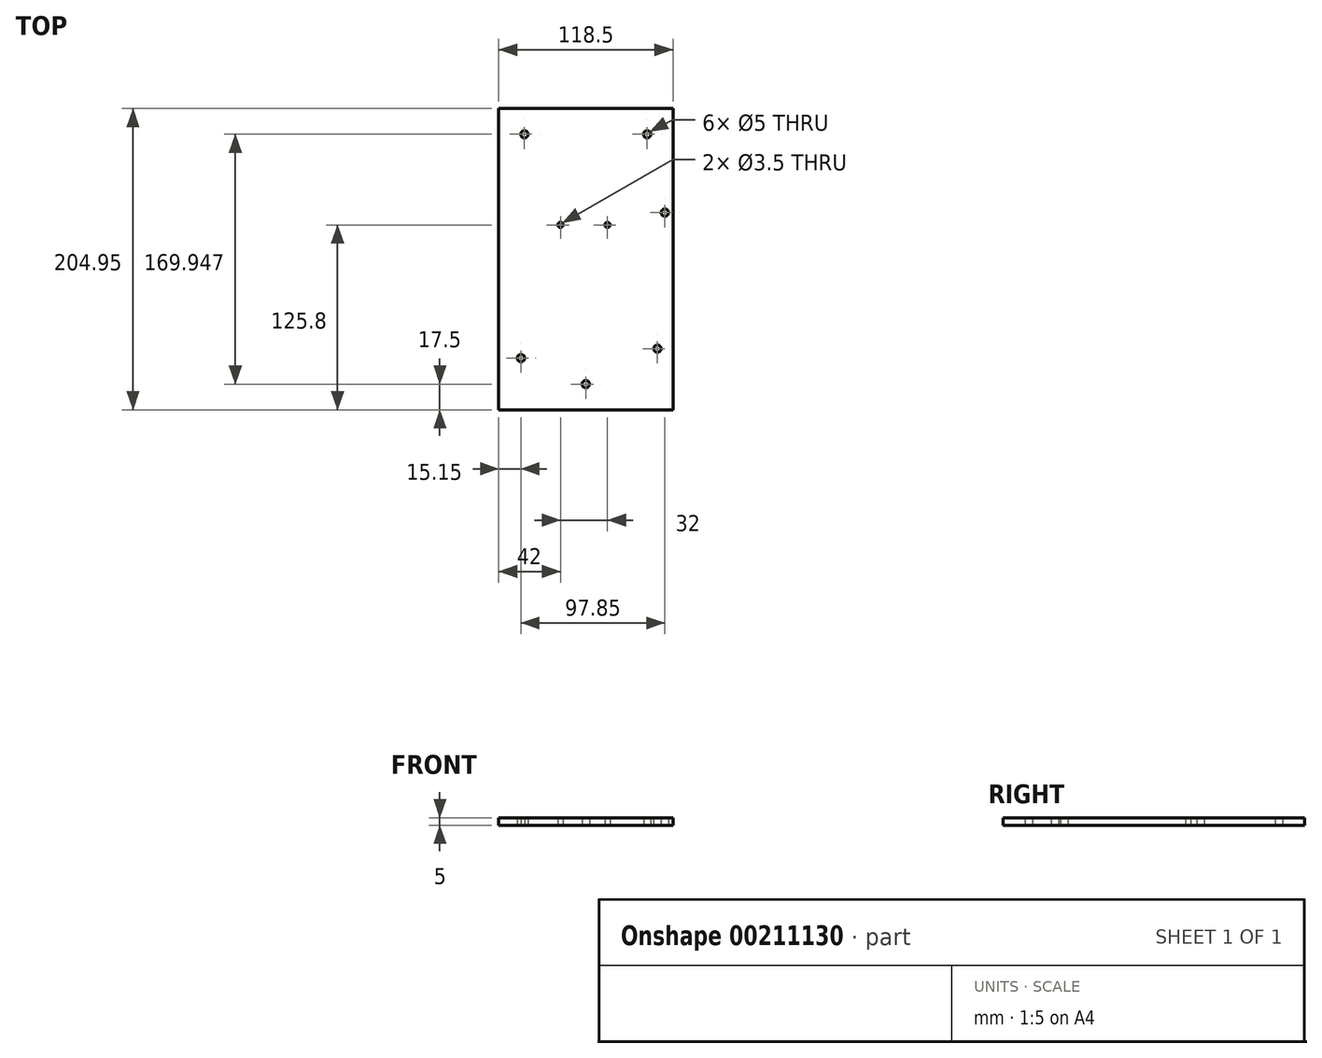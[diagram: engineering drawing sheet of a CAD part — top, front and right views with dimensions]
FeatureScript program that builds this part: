
annotation { "Feature Type Name" : "Feature", "Feature Type Description" : "" }
export const myFeature = defineFeature(function(context is Context, id is Id, definition is map)
    precondition{}
    {
        {
            var Q0;
            Q0=qCreatedBy(makeId("Top.planeOp"),FACE);
            var sketch = newSketch(context, id + "F0", { "sketchPlane" : qUnion([Q0])});
            skLineSegment(sketch, "E0", {"start": v(0, 0) * mm, "end": v(41.75, 169.95) * mm, "construction": true});
            skLineSegment(sketch, "E1", {"start": v(41.75, 169.95) * mm, "end": v(-41.75, 169.95) * mm, "construction": true});
            skLineSegment(sketch, "E2", {"start": v(-41.75, 169.95) * mm, "end": v(0, 0) * mm, "construction": true});
            skCircle(sketch, "E3", {"center": v(-41.75, 169.95) * mm, "radius": 2.25 * mm});
            skCircle(sketch, "E4", {"center": v(41.75, 169.95) * mm, "radius": 2.25 * mm});
            skCircle(sketch, "E5", {"center": v(0, 0) * mm, "radius": 2.25 * mm});
            skSolve(sketch);
        }
        {
            var Q0;
            Q0=qCreatedBy(makeId("Top.planeOp"),FACE);
            var sketch = newSketch(context, id + "F1", { "sketchPlane" : qUnion([Q0])});
            skLineSegment(sketch, "E6.bottom", {"start": v(-49.25, 30) * mm, "end": v(49.25, 30) * mm});
            skLineSegment(sketch, "E6.top", {"start": v(-49.25, 160) * mm, "end": v(49.25, 160) * mm});
            skLineSegment(sketch, "E6.left", {"start": v(-49.25, 30) * mm, "end": v(-49.25, 160) * mm});
            skLineSegment(sketch, "E6.right", {"start": v(49.25, 30) * mm, "end": v(49.25, 160) * mm});
            skCircle(sketch, "E7", {"center": v(-17.25, 108.3) * mm, "radius": 1.5 * mm});
            skCircle(sketch, "E8", {"center": v(14.75, 108.3) * mm, "radius": 1.5 * mm});
            skLineSegment(sketch, "E9", {"start": v(0, 30) * mm, "end": v(0, 0) * mm, "construction": true});
            skSolve(sketch);
        }
        {
            var Q0;
            Q0=qCreatedBy(makeId("Top.planeOp"),FACE);
            var sketch = newSketch(context, id + "F2", { "sketchPlane" : qUnion([Q0])});
            skLineSegment(sketch, "E10.bottom", {"start": v(-47.5, 144.58) * mm, "end": v(57.5, 144.58) * mm});
            skLineSegment(sketch, "E10.top", {"start": v(-47.5, 15) * mm, "end": v(57.5, 15) * mm});
            skLineSegment(sketch, "E10.left", {"start": v(-47.5, 144.58) * mm, "end": v(-47.5, 15) * mm});
            skLineSegment(sketch, "E10.right", {"start": v(57.5, 144.58) * mm, "end": v(57.5, 15) * mm});
            skCircle(sketch, "E11", {"center": v(-44.2, 116.78) * mm, "radius": 1.8 * mm});
            skCircle(sketch, "E12", {"center": v(53.75, 116.68) * mm, "radius": 1.8 * mm});
            skCircle(sketch, "E13", {"center": v(48.7, 24.1) * mm, "radius": 1.8 * mm});
            skCircle(sketch, "E14", {"center": v(-44.1, 17.7) * mm, "radius": 1.8 * mm});
            skSolve(sketch);
        }
        {
            var Q0;
            Q0=qCreatedBy(makeId("Top.planeOp"),FACE);
            var sketch = newSketch(context, id + "F3", { "sketchPlane" : qUnion([Q0])});
            skLineSegment(sketch, "E15.bottom", {"start": v(-59.25, -17.5) * mm, "end": v(59.25, -17.5) * mm});
            skLineSegment(sketch, "E15.top", {"start": v(-59.25, 187.45) * mm, "end": v(59.25, 187.45) * mm});
            skLineSegment(sketch, "E15.left", {"start": v(-59.25, -17.5) * mm, "end": v(-59.25, 187.45) * mm});
            skLineSegment(sketch, "E15.right", {"start": v(59.25, -17.5) * mm, "end": v(59.25, 187.45) * mm});
            skPoint(sketch, "E16.0", {"position": v(-44.1, 17.7) * mm});
            skPoint(sketch, "E17.0", {"position": v(48.7, 24.1) * mm});
            skPoint(sketch, "E18.0", {"position": v(53.75, 116.68) * mm});
            skPoint(sketch, "E19.0", {"position": v(14.75, 108.3) * mm});
            skPoint(sketch, "E20.0", {"position": v(-17.25, 108.3) * mm});
            skPoint(sketch, "E21.0", {"position": v(-41.75, 169.95) * mm});
            skPoint(sketch, "E22.0", {"position": v(41.75, 169.95) * mm});
            skPoint(sketch, "E23.0", {"position": v(0, 0) * mm});
            skCircle(sketch, "E24", {"center": v(53.75, 116.68) * mm, "radius": 2.5 * mm});
            skCircle(sketch, "E25", {"center": v(48.7, 24.1) * mm, "radius": 2.5 * mm});
            skCircle(sketch, "E26", {"center": v(-44.1, 17.7) * mm, "radius": 2.5 * mm});
            skCircle(sketch, "E27", {"center": v(-17.25, 108.3) * mm, "radius": 1.75 * mm});
            skCircle(sketch, "E28", {"center": v(14.75, 108.3) * mm, "radius": 1.75 * mm});
            skCircle(sketch, "E29", {"center": v(-41.75, 169.95) * mm, "radius": 2.5 * mm});
            skCircle(sketch, "E30", {"center": v(41.75, 169.95) * mm, "radius": 2.5 * mm});
            skCircle(sketch, "E31", {"center": v(0, 0) * mm, "radius": 2.5 * mm});
            skLineSegment(sketch, "E32", {"start": v(-44.25, 169.95) * mm, "end": v(-59.25, 169.95) * mm, "construction": true});
            skLineSegment(sketch, "E33", {"start": v(-41.75, 172.45) * mm, "end": v(-41.75, 187.45) * mm, "construction": true});
            skLineSegment(sketch, "E34", {"start": v(44.25, 169.95) * mm, "end": v(59.25, 169.95) * mm, "construction": true});
            skLineSegment(sketch, "E35", {"start": v(0, -2.5) * mm, "end": v(0, -17.5) * mm, "construction": true});
            skSolve(sketch);
        }
        {
            var Q0;
            Q0=makeQuery(id+"F3.imprint","IMPRINT",FACE,{"disambiguationData":[TD([[makeQuery(id+"F3.imprint","IMPRINT",EDGE,{"derivedFrom":sQuery(id+"F3.wireOp",EDGE,"E15.bottom")}),1.0]])]});
            extrude(context, id + "F4", {"entities" : qUnion([Q0]), "depth" : 5 * mm});
        }
    });
